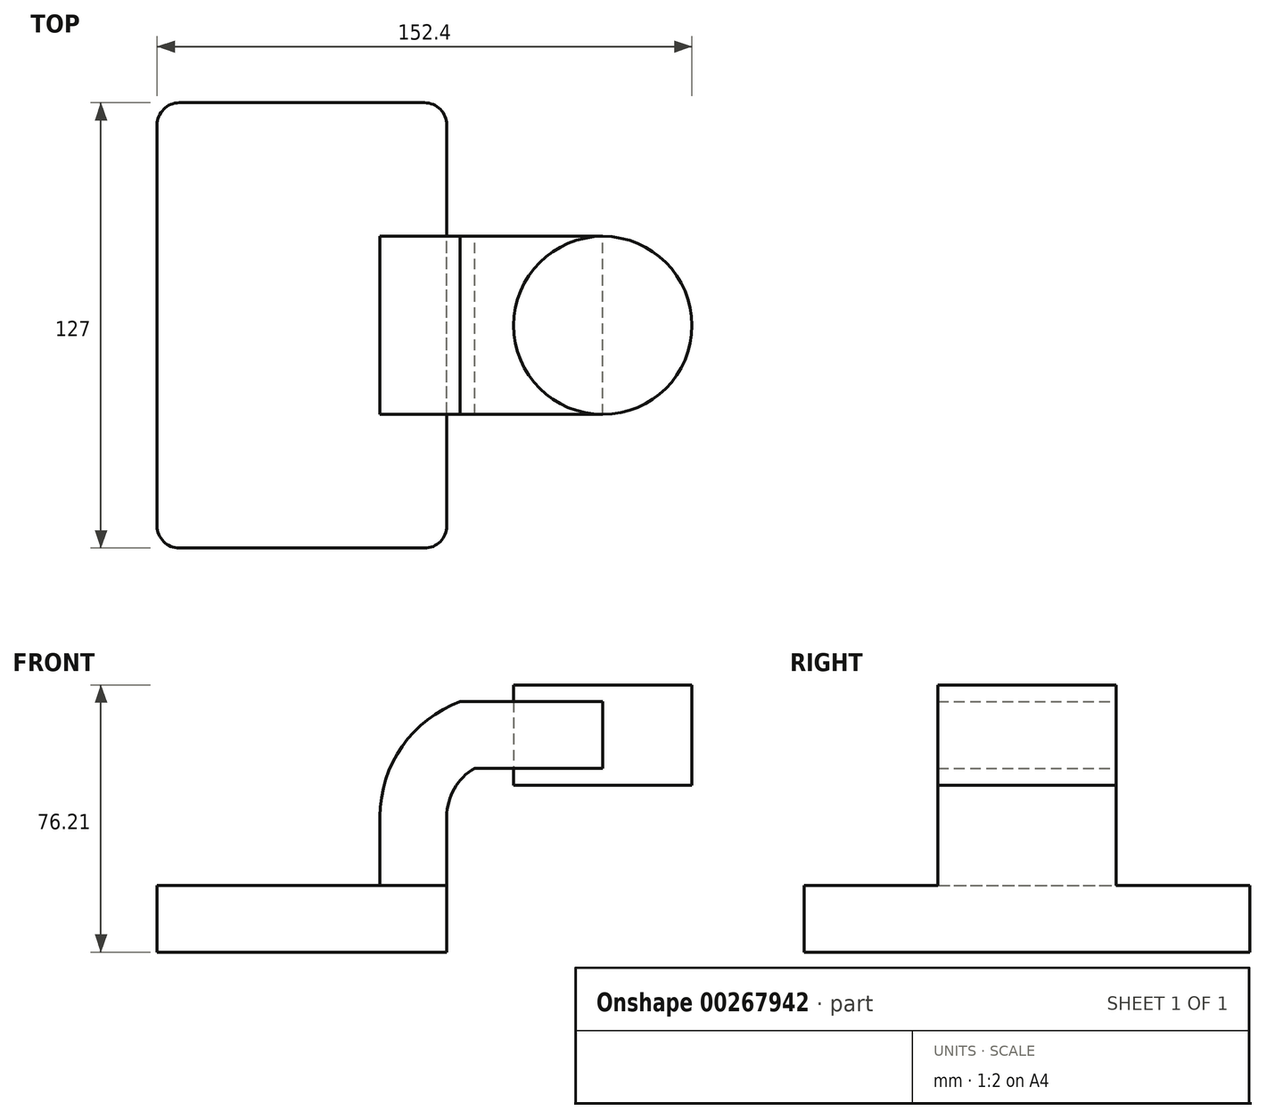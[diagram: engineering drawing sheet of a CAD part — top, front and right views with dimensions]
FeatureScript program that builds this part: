
annotation { "Feature Type Name" : "Feature", "Feature Type Description" : "" }
export const myFeature = defineFeature(function(context is Context, id is Id, definition is map)
    precondition{}
    {
        {
            var Q0;
            Q0=qCreatedBy(makeId("Front.planeOp"),FACE);
            var sketch = newSketch(context, id + "F0", { "sketchPlane" : qUnion([Q0])});
            skLineSegment(sketch, "E0.bottom", {"start": v(-41.28, 9.52) * mm, "end": v(41.28, 9.53) * mm});
            skLineSegment(sketch, "E0.top", {"start": v(-41.28, -9.52) * mm, "end": v(41.28, -9.52) * mm});
            skLineSegment(sketch, "E0.left", {"start": v(-41.28, 9.52) * mm, "end": v(-41.28, -9.53) * mm});
            skLineSegment(sketch, "E0.right", {"start": v(41.27, 9.53) * mm, "end": v(41.28, -9.52) * mm});
            skPoint(sketch, "E0.middle", {"position": v(0, 0) * mm});
            skLineSegment(sketch, "E1.bottom", {"start": v(60.32, 66.68) * mm, "end": v(111.12, 66.68) * mm});
            skLineSegment(sketch, "E1.top", {"start": v(60.32, 38.1) * mm, "end": v(111.12, 38.1) * mm});
            skLineSegment(sketch, "E1.left", {"start": v(60.32, 66.68) * mm, "end": v(60.32, 38.1) * mm});
            skLineSegment(sketch, "E1.right", {"start": v(111.12, 66.68) * mm, "end": v(111.13, 38.1) * mm});
            skPoint(sketch, "E1.middle", {"position": v(85.72, 52.39) * mm});
            skLineSegment(sketch, "E2", {"start": v(41.27, 9.53) * mm, "end": v(41.27, 29.14) * mm});
            skArc(sketch, "E3", {"start": v(41.28, 29.14) * mm, "mid": v(43.4, 37.07) * mm, "end": v(49.2, 42.88) * mm});
            skLineSegment(sketch, "E4", {"start": v(49.2, 42.88) * mm, "end": v(85.72, 42.88) * mm});
            skLineSegment(sketch, "E5.0", {"start": v(45.12, 61.93) * mm, "end": v(85.72, 61.93) * mm});
            skArc(sketch, "E5.1", {"start": v(22.23, 29.14) * mm, "mid": v(28.52, 49.13) * mm, "end": v(45.12, 61.93) * mm});
            skLineSegment(sketch, "E5.2", {"start": v(22.22, 9.53) * mm, "end": v(22.22, 29.14) * mm});
            skLineSegment(sketch, "E6", {"start": v(85.72, 38.1) * mm, "end": v(85.72, 66.68) * mm});
            skFitSpline(sketch, "E7", {"points": [v(-41.28, 9.52) * mm, v(45.12, 61.93) * mm], "startDerivative": vector(63.33, 57.4) * mm, "endDerivative": vector(122.6, -2.2) * mm});
            skSolve(sketch);
        }
        {
            var Q0;
            Q0=makeQuery(id+"F0.imprint","IMPRINT",FACE,{"disambiguationData":[TD([[makeQuery(id+"F0.imprint","IMPRINT",EDGE,{"derivedFrom":sQuery(id+"F0.wireOp",EDGE,"E0.top")}),1.0]])]});
            extrude(context, id + "F1", {"entities" : qUnion([Q0]), "endBound" : BoundingType.SYMMETRIC, "depth" : 127 * mm});
        }
        {
            var Q0;
            {var subQ1=sQuery(id+"F0.wireOp",EDGE,"E2");Q0=makeQuery(id+"F0.imprint","IMPRINT",FACE,{"disambiguationData":[TD([[makeQuery(id+"F0.imprint","IMPRINT",EDGE,{"derivedFrom":subQ1}),1.0]])]});}
            var Q1;
            {var subQ0=sQuery(id+"F0.wireOp",EDGE,"E5.0");var subQ1=sQuery(id+"F0.wireOp",EDGE,"E1.left");var subQ2=makeQuery(id+"F0.imprint","INTERSECT",VERTEX,{"derivedFrom":[subQ1,subQ0]});Q1=makeQuery(id+"F0.imprint","IMPRINT",FACE,{"disambiguationData":[TD([[makeQuery(id+"F0.imprint","IMPRINT",EDGE,{"disambiguationData":[TD([[subQ2,-1.0]])],"derivedFrom":subQ1}),1.0]])]});}
            extrude(context, id + "F2", {"entities" : qUnion([Q0, Q1]), "operationType" : NewBodyOperationType.ADD, "endBound" : BoundingType.SYMMETRIC, "depth" : 50.8 * mm});
        }
        {
            var Q0;
            Q0=makeQuery(id+"F0.imprint","IMPRINT",FACE,{"disambiguationData":[TD([[makeQuery(id+"F0.imprint","IMPRINT",EDGE,{"derivedFrom":sQuery(id+"F0.wireOp",EDGE,"E5.1")}),1.0]])]});
            extrude(context, id + "F3", {"entities" : qUnion([Q0]), "operationType" : NewBodyOperationType.ADD, "endBound" : BoundingType.SYMMETRIC, "depth" : 15.88 * mm});
        }
        {
            var Q0;
            {var subQ0=sQuery(id+"F0.wireOp",EDGE,"E1.right");Q0=makeQuery(id+"F0.imprint","IMPRINT",FACE,{"disambiguationData":[TD([[makeQuery(id+"F0.imprint","IMPRINT",EDGE,{"derivedFrom":subQ0}),-1.0]])]});}
            var Q1;
            Q1=sQuery(id+"F0.wireOp",EDGE,"E6");
            revolve(context, id + "F4", {"entities" : qUnion([Q0]), "axis" : qUnion([Q1]), "revolveType" : RevolveType.FULL});
        }
        {
            var Q0;
            Q0=makeQuery(id+"F1.opExtrude","CAP_EDGE",EDGE,{"disambiguationData":[OSD([sQuery(id+"F0.wireOp",EDGE,"E0.left")])],"isStart":false});
            var Q1;
            Q1=makeQuery(id+"F1.opExtrude","CAP_EDGE",EDGE,{"disambiguationData":[OSD([sQuery(id+"F0.wireOp",EDGE,"E0.right")])],"isStart":false});
            var Q2;
            Q2=makeQuery(id+"F1.opExtrude","CAP_EDGE",EDGE,{"disambiguationData":[OSD([sQuery(id+"F0.wireOp",EDGE,"E0.left")])],"isStart":true});
            var Q3;
            Q3=makeQuery(id+"F1.opExtrude","CAP_EDGE",EDGE,{"disambiguationData":[OSD([sQuery(id+"F0.wireOp",EDGE,"E0.right")])],"isStart":true});
            fillet(context, id + "F5", {"entities" : qUnion([Q0, Q1, Q2, Q3]), "radius" : 6.35 * mm, "tangentPropagation" : true, "allowEdgeOverflow" : false});
        }
    });
